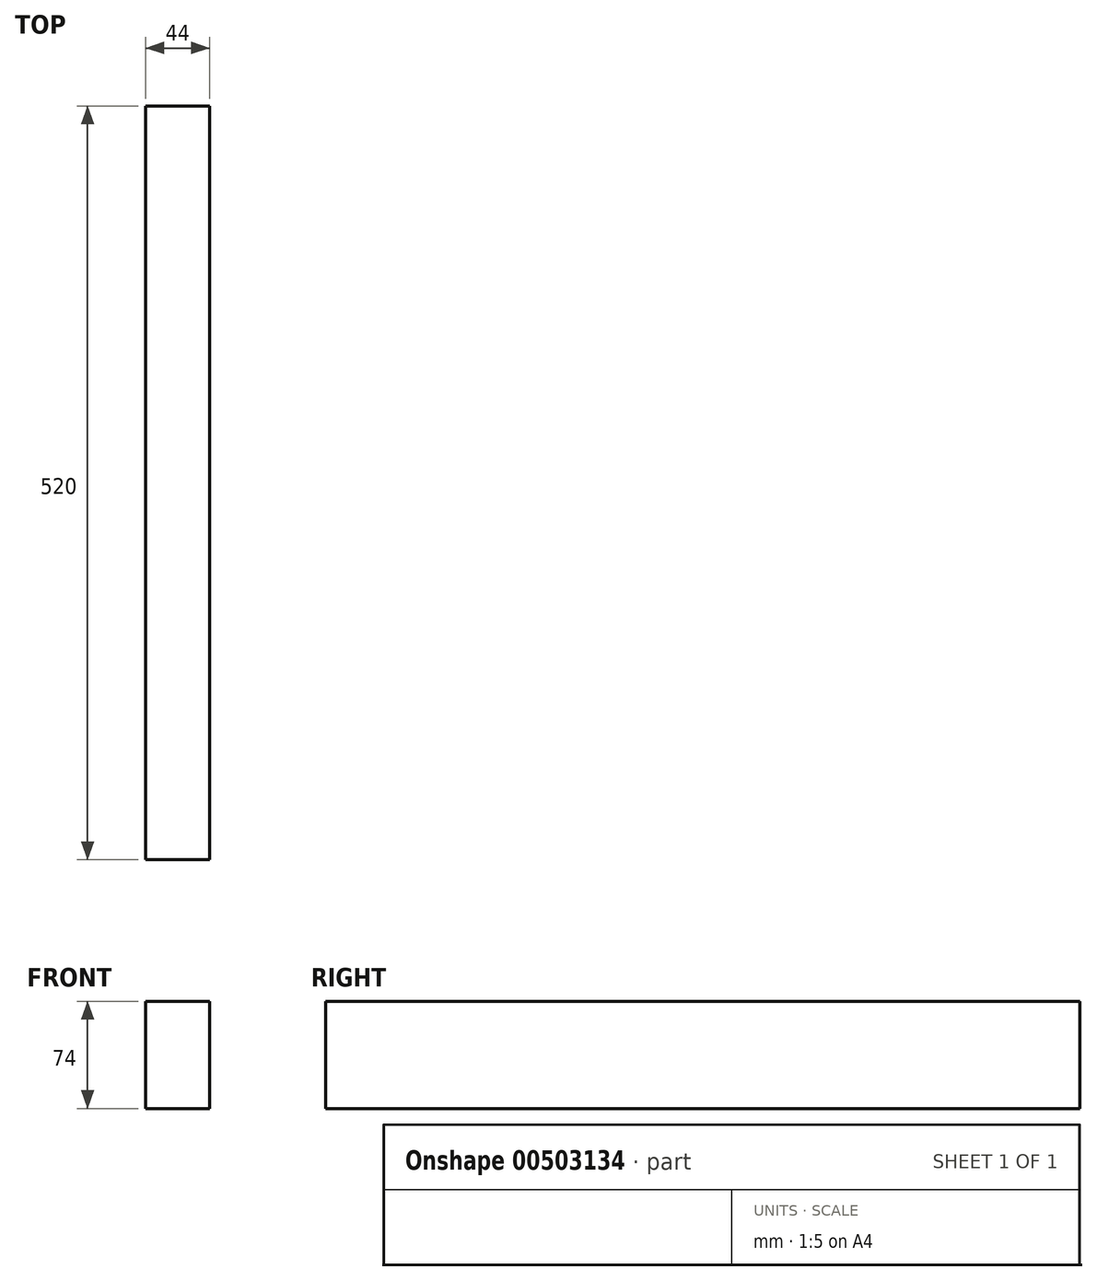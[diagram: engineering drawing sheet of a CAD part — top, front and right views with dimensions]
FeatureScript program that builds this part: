
annotation { "Feature Type Name" : "Feature", "Feature Type Description" : "" }
export const myFeature = defineFeature(function(context is Context, id is Id, definition is map)
    precondition{}
    {
        {
            var Q0;
            Q0=qCreatedBy(makeId("Right.planeOp"),FACE);
            var sketch = newSketch(context, id + "F0", { "sketchPlane" : qUnion([Q0])});
            skLineSegment(sketch, "E0.bottom", {"start": v(-377.87, -66.92) * mm, "end": v(142.13, -66.92) * mm});
            skLineSegment(sketch, "E0.top", {"start": v(-377.87, -140.92) * mm, "end": v(142.13, -140.92) * mm});
            skLineSegment(sketch, "E0.left", {"start": v(-377.87, -66.92) * mm, "end": v(-377.87, -140.92) * mm});
            skLineSegment(sketch, "E0.right", {"start": v(142.13, -66.92) * mm, "end": v(142.13, -140.92) * mm});
            skSolve(sketch);
        }
        {
            var Q0;
            Q0 = qSketchRegion(id + "F0", true);
            extrude(context, id + "F1", {"entities" : qUnion([Q0]), "depth" : 44 * mm, "offsetDistance" : 25 * mm});
        }
    });
